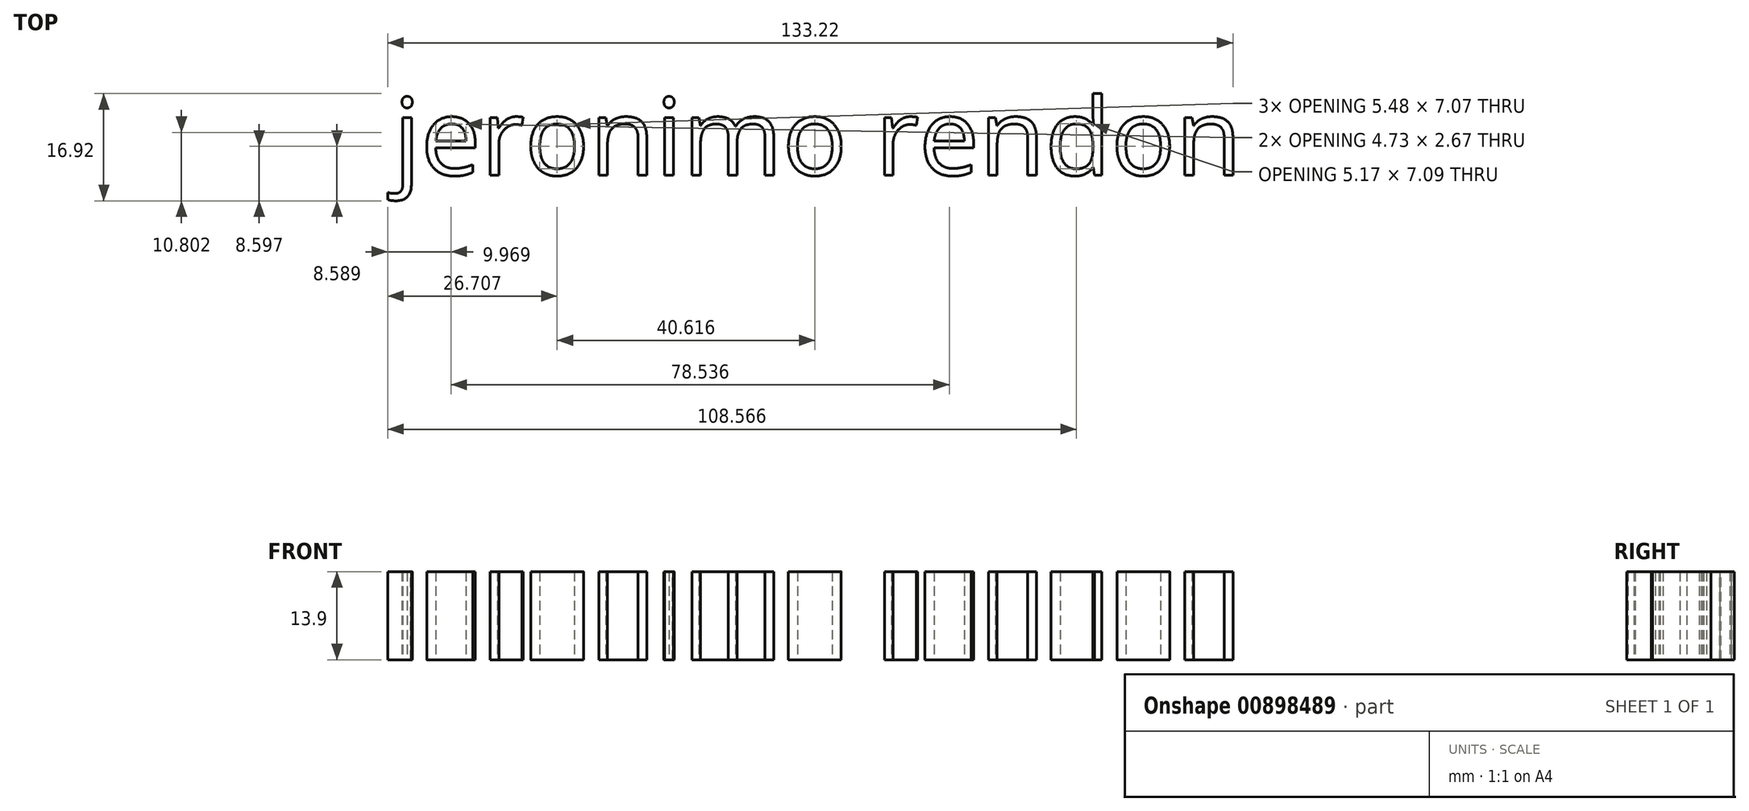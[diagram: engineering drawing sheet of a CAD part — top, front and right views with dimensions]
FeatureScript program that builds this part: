
annotation { "Feature Type Name" : "Feature", "Feature Type Description" : "" }
export const myFeature = defineFeature(function(context is Context, id is Id, definition is map)
    precondition{}
    {
        {
            var Q0;
            Q0=qCreatedBy(makeId("Top.planeOp"),FACE);
            var sketch = newSketch(context, id + "F0", { "sketchPlane" : qUnion([Q0])});
            skText(sketch, "E0", { "text": "jeronimo rendon", "fontName": "OpenSans-Regular.ttf"});
            const initialGuessF0  = {"E0": [-0.06586, 0.03923, 1, 0, 0.01218]};
            skSetInitialGuess(sketch, initialGuessF0);
            skSolve(sketch);
        }
        {
            var Q0;
            Q0 = qSketchRegion(id + "F0", true);
            extrude(context, id + "F1", {"entities" : qUnion([Q0]), "depth" : 13.9 * mm, "offsetDistance" : 25 * mm});
        }
    });
